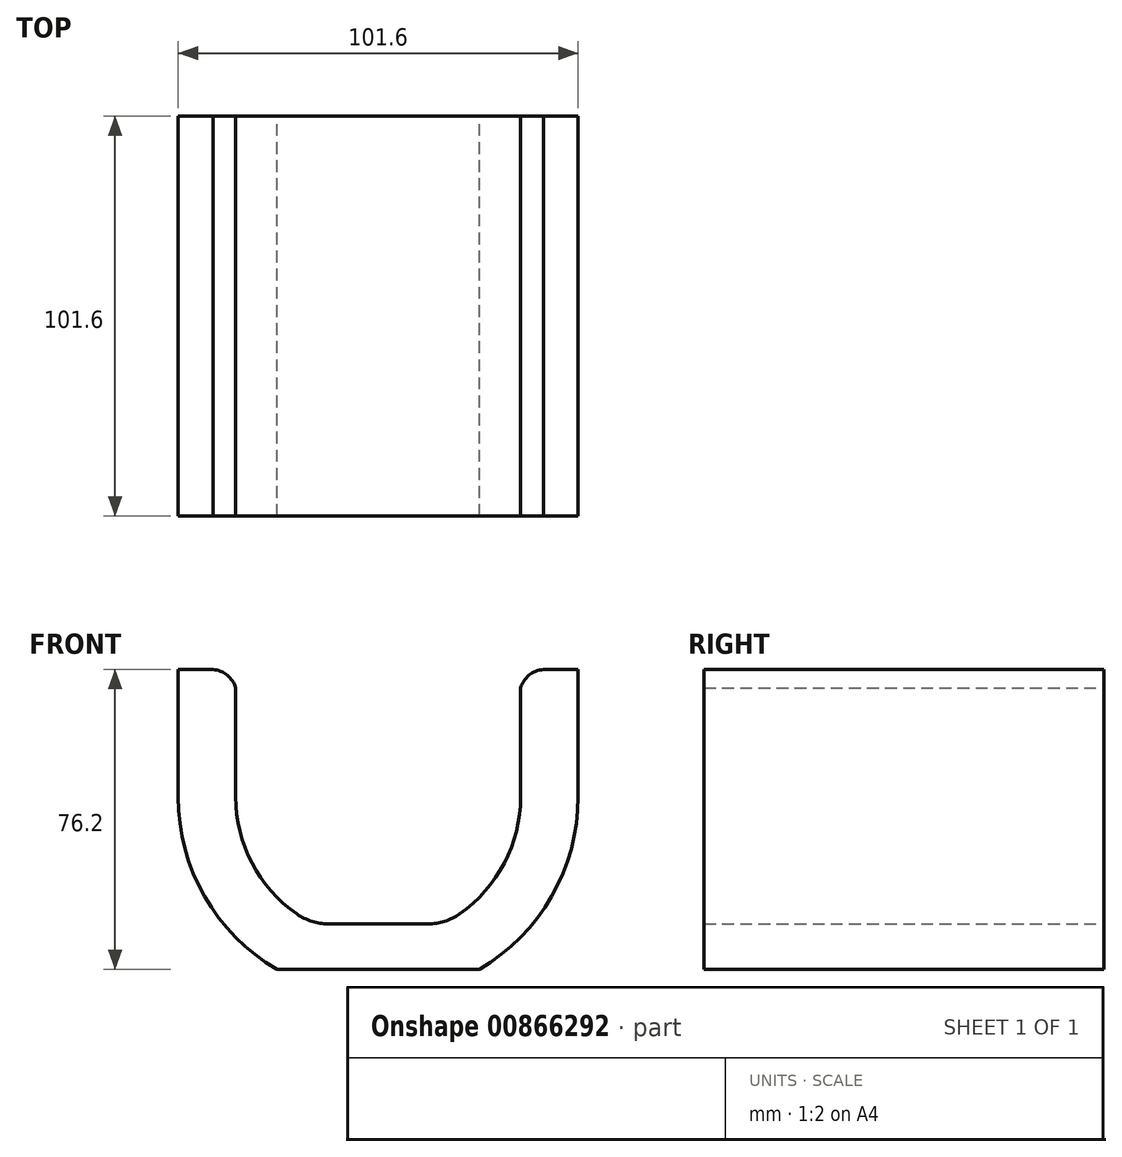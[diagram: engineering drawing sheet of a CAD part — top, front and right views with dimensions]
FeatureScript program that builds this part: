
annotation { "Feature Type Name" : "Feature", "Feature Type Description" : "" }
export const myFeature = defineFeature(function(context is Context, id is Id, definition is map)
    precondition{}
    {
        {
            var Q0;
            Q0=qCreatedBy(makeId("Front.planeOp"),FACE);
            var sketch = newSketch(context, id + "F0", { "sketchPlane" : qUnion([Q0])});
            skArc(sketch, "E0", {"start": v(-36.19, 0) * mm, "mid": v(-32.07, -16.77) * mm, "end": v(-20.64, -29.72) * mm});
            skLineSegment(sketch, "E1", {"start": v(-12.67, -32.22) * mm, "end": v(0, -32.22) * mm});
            skLineSegment(sketch, "E2.top", {"start": v(-25.73, -43.8) * mm, "end": v(0, -43.8) * mm});
            skLineSegment(sketch, "E2.left", {"start": v(-50.8, 32.4) * mm, "end": v(-50.8, 0) * mm});
            skLineSegment(sketch, "E3", {"start": v(-36.19, 0) * mm, "end": v(-36.19, 27.7) * mm});
            skLineSegment(sketch, "E4", {"start": v(-41.98, 32.4) * mm, "end": v(-50.8, 32.4) * mm});
            skArc(sketch, "E5", {"start": v(-36.19, 27.7) * mm, "mid": v(-38.34, 30.97) * mm, "end": v(-41.98, 32.4) * mm});
            skLineSegment(sketch, "E6", {"start": v(0, -32.22) * mm, "end": v(0, -43.8) * mm, "construction": true});
            skPoint(sketch, "E7.visualSharp", {"position": v(-16.48, -32.22) * mm});
            skArc(sketch, "E7.filletArc", {"start": v(-20.64, -29.72) * mm, "mid": v(-16.85, -31.58) * mm, "end": v(-12.67, -32.22) * mm});
            skArc(sketch, "E8.MirrorCS", {"start": v(20.64, -29.72) * mm, "mid": v(16.85, -31.58) * mm, "end": v(12.67, -32.22) * mm});
            skArc(sketch, "E9.MirrorCS", {"start": v(36.19, 27.7) * mm, "mid": v(38.34, 30.97) * mm, "end": v(41.98, 32.4) * mm});
            skLineSegment(sketch, "E10.MirrorCS", {"start": v(41.98, 32.4) * mm, "end": v(50.8, 32.4) * mm});
            skArc(sketch, "E11.MirrorCS", {"start": v(36.19, 0) * mm, "mid": v(32.07, -16.77) * mm, "end": v(20.64, -29.72) * mm});
            skLineSegment(sketch, "E12.MirrorCS", {"start": v(25.73, -43.8) * mm, "end": v(0, -43.8) * mm});
            skLineSegment(sketch, "E13.MirrorCS", {"start": v(12.67, -32.22) * mm, "end": v(0, -32.22) * mm});
            skPoint(sketch, "E14.MirrorP", {"position": v(16.48, -32.22) * mm});
            skLineSegment(sketch, "E15.MirrorCS", {"start": v(36.19, 0) * mm, "end": v(36.19, 27.7) * mm});
            skLineSegment(sketch, "E16.MirrorCS", {"start": v(50.8, 32.4) * mm, "end": v(50.8, 0) * mm});
            skArc(sketch, "E17", {"start": v(-50.8, 0) * mm, "mid": v(-44.09, -25.24) * mm, "end": v(-25.73, -43.8) * mm});
            skArc(sketch, "E18.trimOffspring", {"start": v(25.73, -43.8) * mm, "mid": v(44.09, -25.24) * mm, "end": v(50.8, 0) * mm});
            skSolve(sketch);
        }
        {
            var Q0;
            Q0=makeQuery(id+"F0.imprint","IMPRINT",FACE,{"disambiguationData":[TD([[makeQuery(id+"F0.imprint","IMPRINT",EDGE,{"derivedFrom":sQuery(id+"F0.wireOp",EDGE,"E0")}),-1.0]])]});
            extrude(context, id + "F1", {"entities" : qUnion([Q0]), "depth" : 101.6 * mm, "offsetDistance" : 25.4 * mm});
        }
    });
